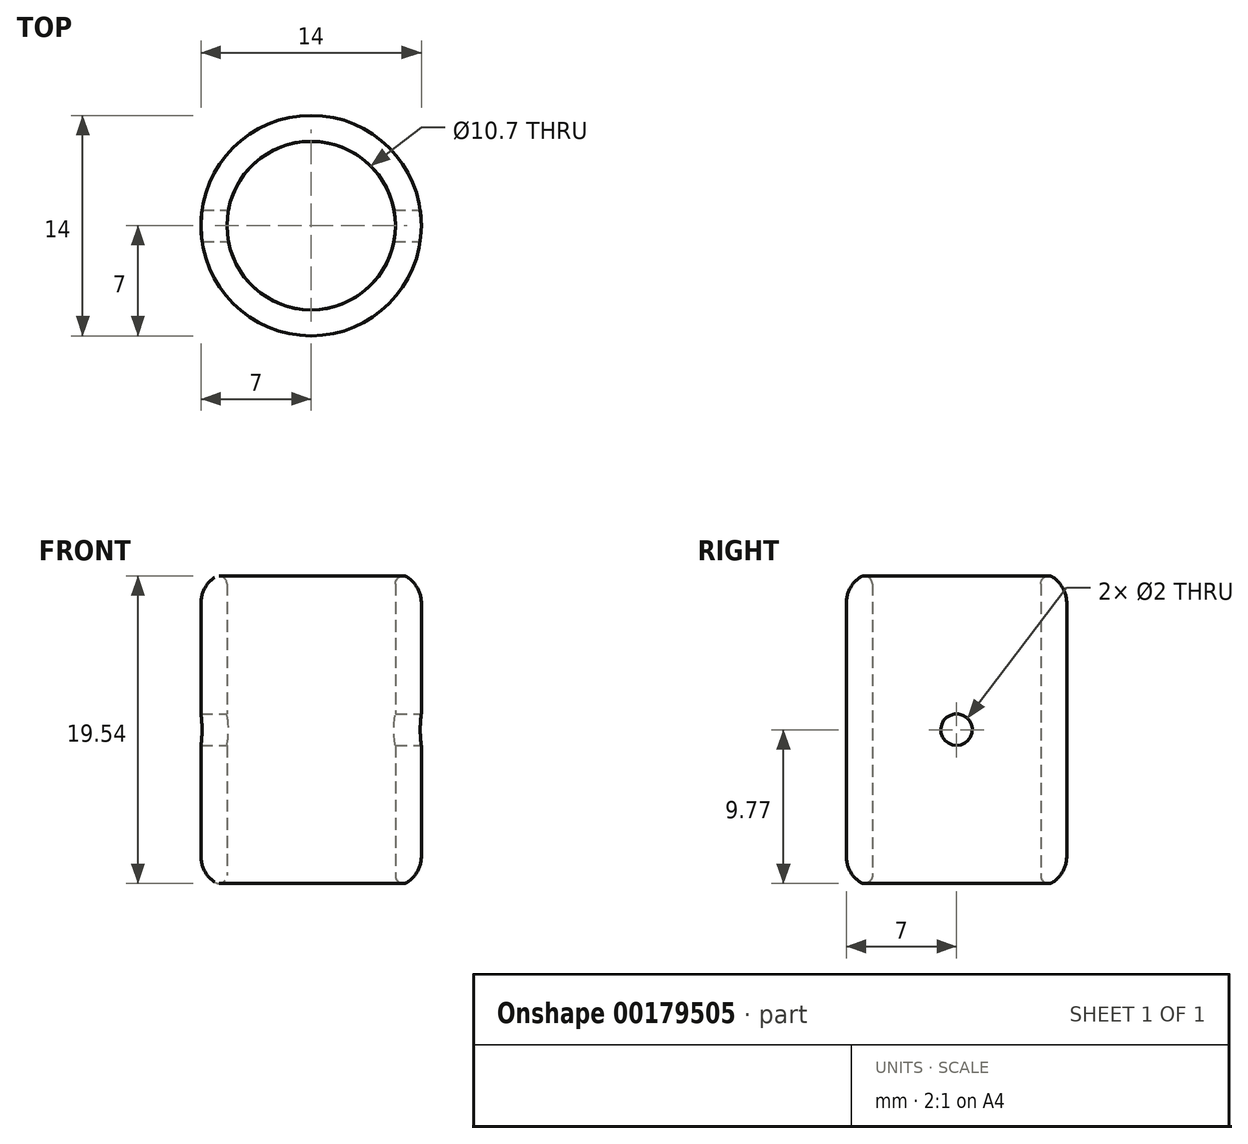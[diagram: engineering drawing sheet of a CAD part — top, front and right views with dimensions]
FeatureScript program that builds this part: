
annotation { "Feature Type Name" : "Feature", "Feature Type Description" : "" }
export const myFeature = defineFeature(function(context is Context, id is Id, definition is map)
    precondition{}
    {
        {
            var Q0;
            Q0=qCreatedBy(makeId("Top.planeOp"),FACE);
            var sketch = newSketch(context, id + "F0", { "sketchPlane" : qUnion([Q0])});
            skCircle(sketch, "E0", {"center": v(0, 0) * mm, "radius": 7 * mm});
            skCircle(sketch, "E1", {"center": v(0, 0) * mm, "radius": 5.35 * mm});
            skSolve(sketch);
        }
        {
            var Q0;
            Q0 = qSketchRegion(id + "F0", true);
            extrude(context, id + "F1", {"entities" : qUnion([Q0]), "depth" : 20 * mm});
        }
        {
            var Q0;
            Q0=qCreatedBy(makeId("Right.planeOp"),FACE);
            var sketch = newSketch(context, id + "F2", { "sketchPlane" : qUnion([Q0])});
            skCircle(sketch, "E2", {"center": v(0, 10) * mm, "radius": 1 * mm});
            skSolve(sketch);
        }
        {
            var Q0;
            Q0=makeQuery(id+"F2.imprint","IMPRINT",FACE,{"disambiguationData":[TD([[makeQuery(id+"F2.imprint","IMPRINT",EDGE,{"derivedFrom":sQuery(id+"F2.wireOp",EDGE,"E2")}),1.0]])]});
            extrude(context, id + "F3", {"entities" : qUnion([Q0]), "operationType" : NewBodyOperationType.REMOVE, "endBound" : BoundingType.SYMMETRIC, "oppositeDirection" : true, "depth" : 25 * mm});
        }
        {
            var Q0;
            Q0=makeQuery(id+"F1.opExtrude","CAP_EDGE",EDGE,{"disambiguationData":[OSD([sQuery(id+"F0.wireOp",EDGE,"E0")])],"isStart":false});
            var Q1;
            Q1=makeQuery(id+"F1.opExtrude","CAP_EDGE",EDGE,{"disambiguationData":[OSD([sQuery(id+"F0.wireOp",EDGE,"E0")])],"isStart":true});
            fillet(context, id + "F4", {"entities" : qUnion([Q0, Q1]), "radius" : 2 * mm, "tangentPropagation" : true, "allowEdgeOverflow" : false});
        }
        {
            var Q0;
            Q0=makeQuery(id+"F4.opFillet","BLEND_EDGE",EDGE,{"blendedFrom":[makeQuery(id+"F1.opExtrude","CAP_EDGE",EDGE,{"disambiguationData":[OSD([sQuery(id+"F0.wireOp",EDGE,"E0")])],"isStart":false}),makeQuery(id+"F1.opExtrude","SWEPT_FACE",FACE,{"disambiguationData":[OSD([sQuery(id+"F0.wireOp",EDGE,"E1")])]})],"blendedInto":[makeQuery(id+"F1.opExtrude","SWEPT_FACE",FACE,{"disambiguationData":[OSD([sQuery(id+"F0.wireOp",EDGE,"E1")])]})]});
            var Q1;
            Q1=makeQuery(id+"F4.opFillet","BLEND_EDGE",EDGE,{"blendedFrom":[makeQuery(id+"F1.opExtrude","CAP_EDGE",EDGE,{"disambiguationData":[OSD([sQuery(id+"F0.wireOp",EDGE,"E0")])],"isStart":true}),makeQuery(id+"F1.opExtrude","SWEPT_FACE",FACE,{"disambiguationData":[OSD([sQuery(id+"F0.wireOp",EDGE,"E1")])]})],"blendedInto":[makeQuery(id+"F1.opExtrude","SWEPT_FACE",FACE,{"disambiguationData":[OSD([sQuery(id+"F0.wireOp",EDGE,"E1")])]})]});
            fillet(context, id + "F5", {"entities" : qUnion([Q0, Q1]), "radius" : 0.5 * mm, "tangentPropagation" : true, "allowEdgeOverflow" : false});
        }
    });
